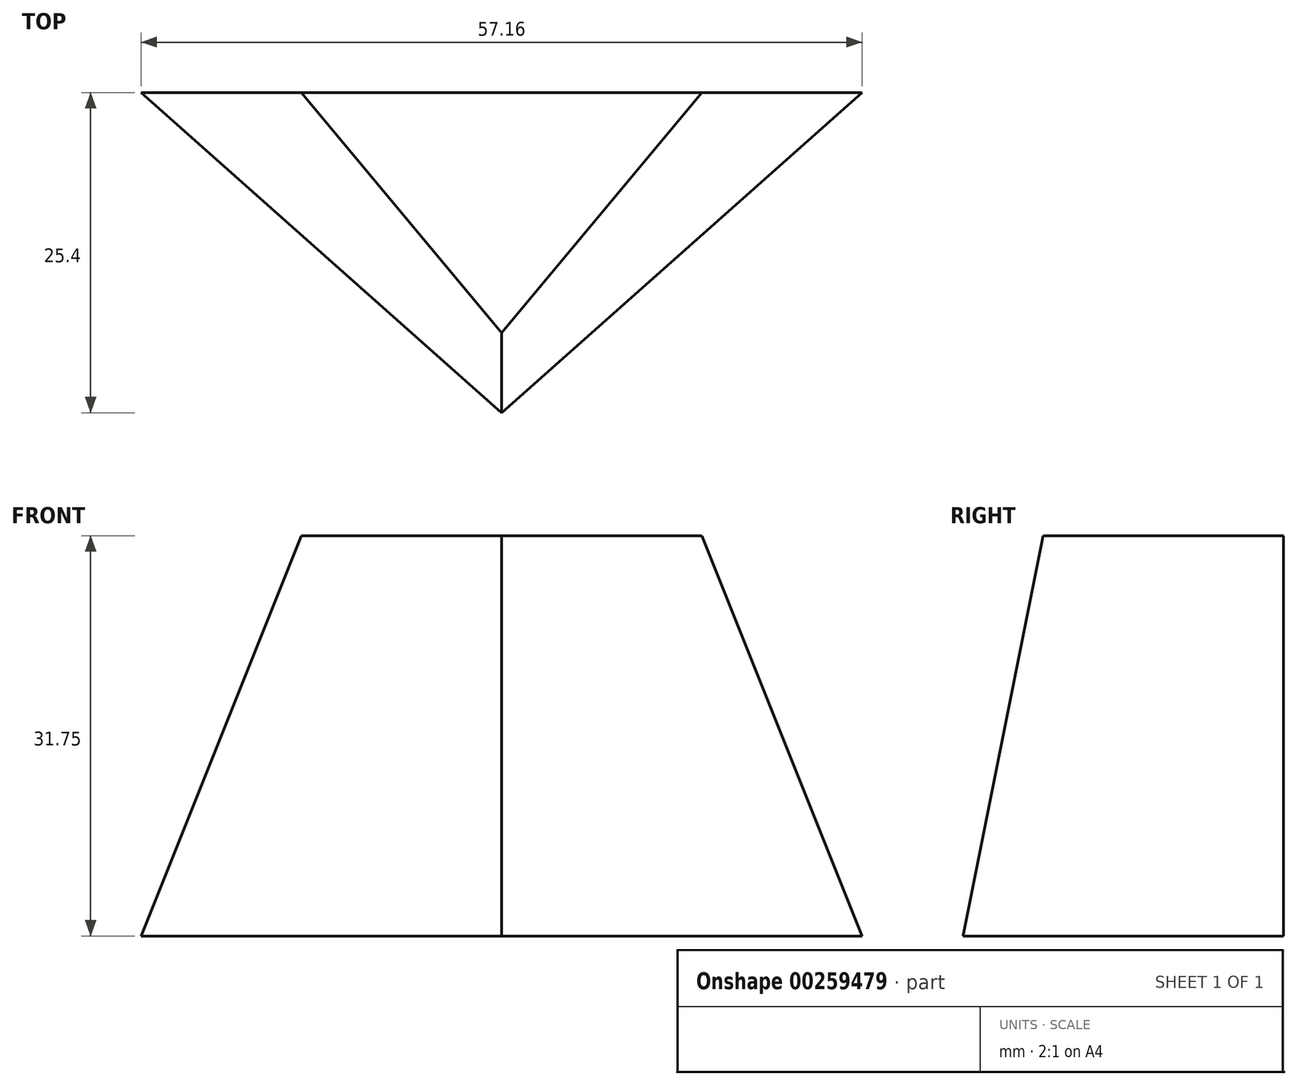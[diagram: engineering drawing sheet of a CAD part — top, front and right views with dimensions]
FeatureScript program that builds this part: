
annotation { "Feature Type Name" : "Feature", "Feature Type Description" : "" }
export const myFeature = defineFeature(function(context is Context, id is Id, definition is map)
    precondition{}
    {
        {
            var Q0;
            Q0=qCreatedBy(makeId("Top.planeOp"),FACE);
            var sketch = newSketch(context, id + "F0", { "sketchPlane" : qUnion([Q0])});
            skLineSegment(sketch, "E0", {"start": v(-15.88, 0) * mm, "end": v(15.88, 0) * mm});
            skLineSegment(sketch, "E1", {"start": v(15.88, 0) * mm, "end": v(0, -19.05) * mm});
            skLineSegment(sketch, "E2", {"start": v(0, -19.05) * mm, "end": v(-15.87, 0) * mm});
            skPoint(sketch, "E3", {"position": v(0, 0) * mm});
            skSolve(sketch);
        }
        {
            var Q0;
            Q0=qCreatedBy(makeId("Top.planeOp"),FACE);
            cPlane(context, id + "F1", {"entities" : qUnion([Q0]), "cplaneType" : CPlaneType.OFFSET, "offset" : 31.75 * mm, "oppositeDirection" : true, "width" : 152.4 * mm, "height" : 152.4 * mm});
        }
        {
            var Q0;
            Q0=qCreatedBy(id+"F1.planeOp",FACE);
            var sketch = newSketch(context, id + "F2", { "sketchPlane" : qUnion([Q0])});
            skLineSegment(sketch, "E4", {"start": v(-28.57, 0) * mm, "end": v(28.57, 0) * mm});
            skLineSegment(sketch, "E5", {"start": v(28.58, 0) * mm, "end": v(0, -25.4) * mm});
            skLineSegment(sketch, "E6", {"start": v(0, -25.4) * mm, "end": v(-28.58, 0) * mm});
            skPoint(sketch, "E7", {"position": v(0, 0) * mm});
            skSolve(sketch);
        }
        {
            var Q0;
            Q0=makeQuery(id+"F0.imprint","IMPRINT",FACE,{"disambiguationData":[TD([[makeQuery(id+"F0.imprint","IMPRINT",EDGE,{"derivedFrom":sQuery(id+"F0.wireOp",EDGE,"E0")}),-1.0]])]});
            var Q1;
            Q1=makeQuery(id+"F2.imprint","IMPRINT",FACE,{"disambiguationData":[TD([[makeQuery(id+"F2.imprint","IMPRINT",EDGE,{"derivedFrom":sQuery(id+"F2.wireOp",EDGE,"E4")}),-1.0]])]});
            loft(context, id + "F3", {"sheetProfilesArray" : [{ "sheetProfileEntities" : qUnion([Q0]) }, { "sheetProfileEntities" : qUnion([Q1]) }]});
        }
    });
